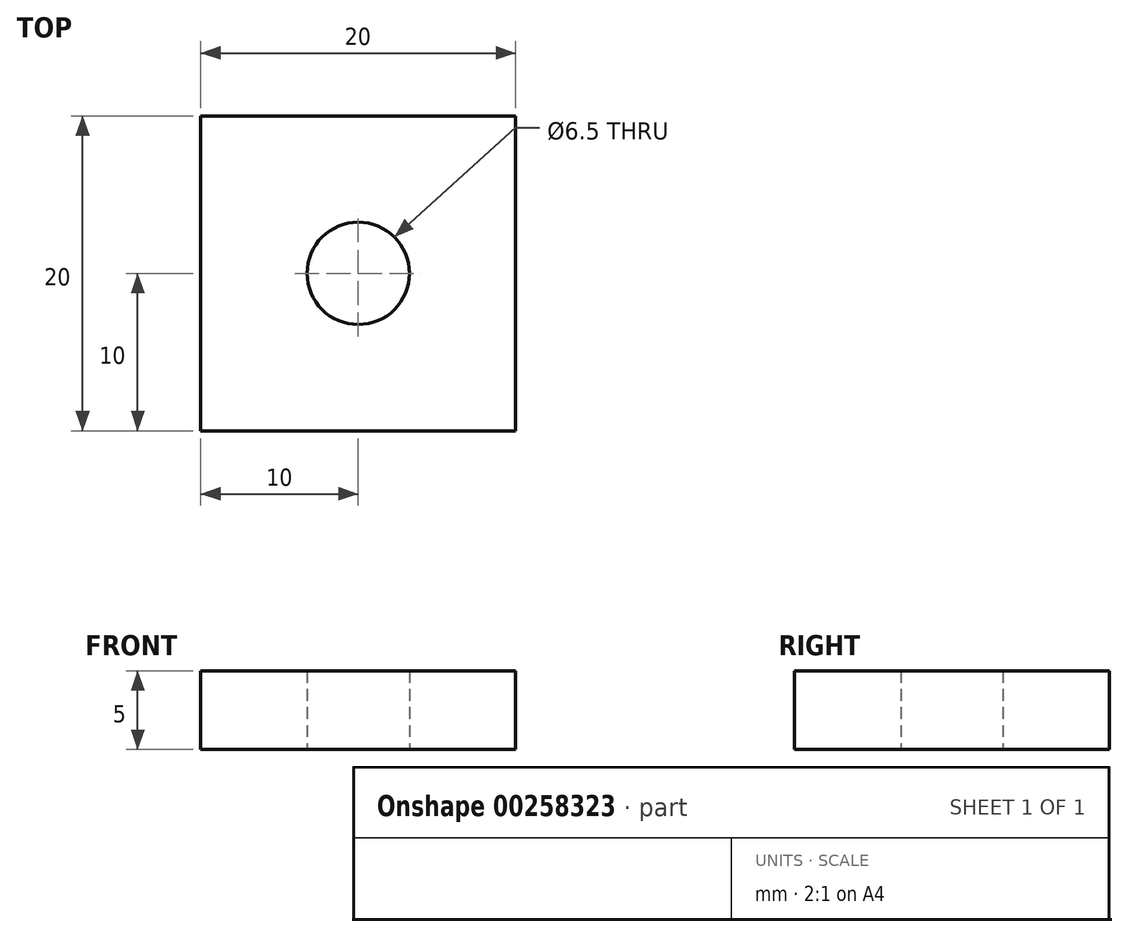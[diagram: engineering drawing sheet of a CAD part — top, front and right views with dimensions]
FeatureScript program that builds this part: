
annotation { "Feature Type Name" : "Feature", "Feature Type Description" : "" }
export const myFeature = defineFeature(function(context is Context, id is Id, definition is map)
    precondition{}
    {
        {
            var Q0;
            Q0=qCreatedBy(makeId("Top.planeOp"),FACE);
            var sketch = newSketch(context, id + "F0", { "sketchPlane" : qUnion([Q0])});
            skLineSegment(sketch, "E0.bottom", {"start": v(10, -10) * mm, "end": v(-10, -10) * mm});
            skLineSegment(sketch, "E0.top", {"start": v(10, 10) * mm, "end": v(-10, 10) * mm});
            skLineSegment(sketch, "E0.left", {"start": v(10, -10) * mm, "end": v(10, 10) * mm});
            skLineSegment(sketch, "E0.right", {"start": v(-10, -10) * mm, "end": v(-10, 10) * mm});
            skPoint(sketch, "E0.middle", {"position": v(0, 0) * mm});
            skCircle(sketch, "E1", {"center": v(0, 0) * mm, "radius": 3.25 * mm});
            skSolve(sketch);
        }
        {
            var Q0;
            Q0 = qSketchRegion(id + "F0", true);
            extrude(context, id + "F1", {"entities" : qUnion([Q0]), "depth" : 5 * mm});
        }
    });
